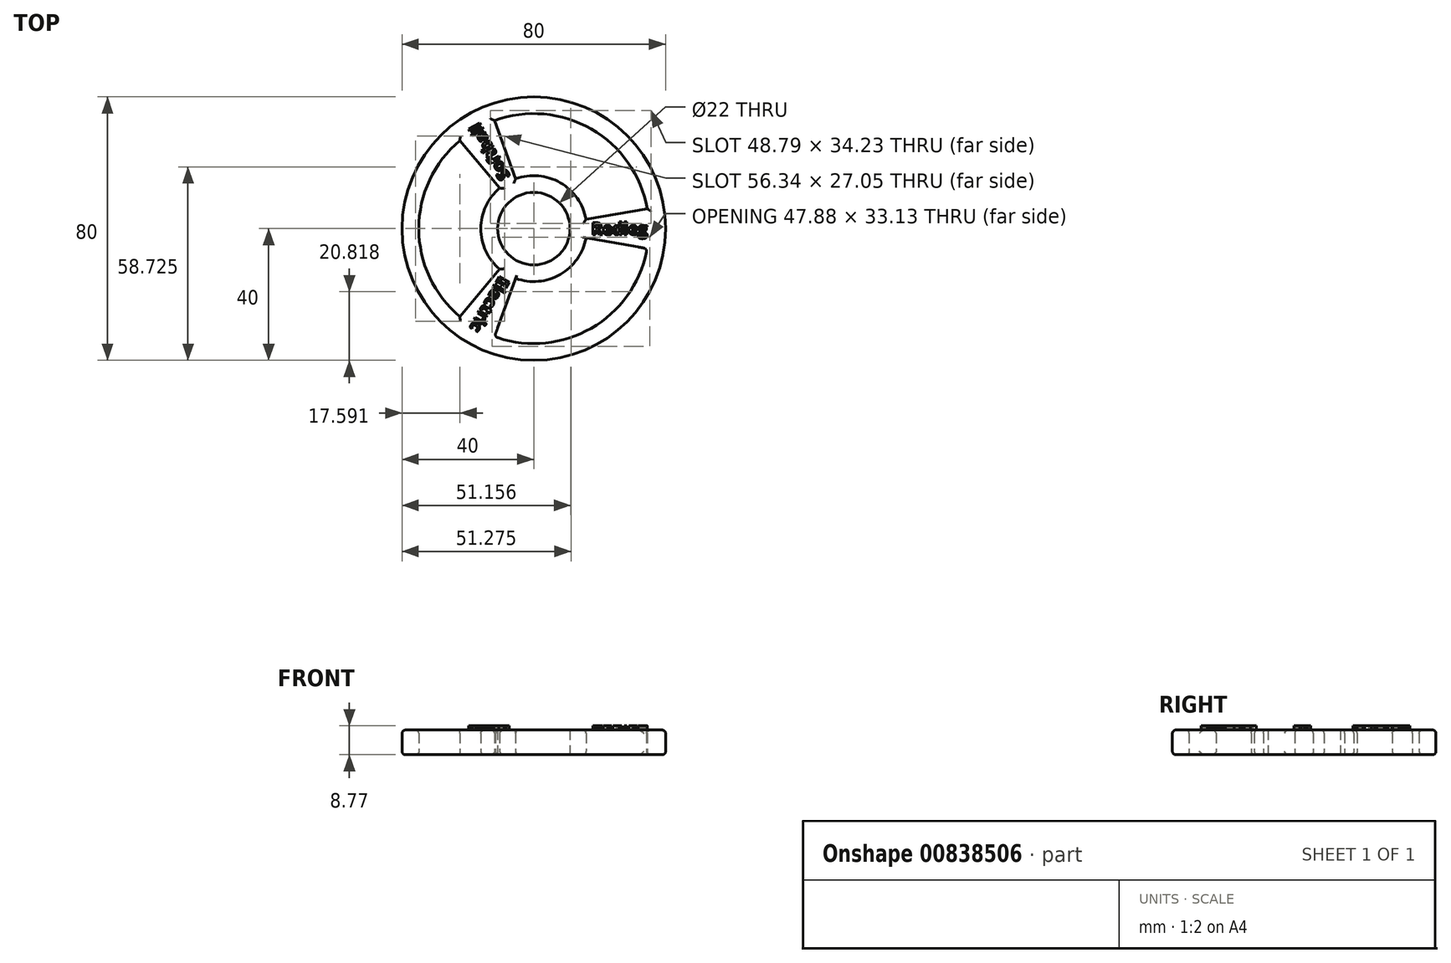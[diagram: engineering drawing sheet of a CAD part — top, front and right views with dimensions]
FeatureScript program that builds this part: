
annotation { "Feature Type Name" : "Feature", "Feature Type Description" : "" }
export const myFeature = defineFeature(function(context is Context, id is Id, definition is map)
    precondition{}
    {
        {
            var Q0;
            Q0=qCreatedBy(makeId("Top.planeOp"),FACE);
            var sketch = newSketch(context, id + "F0", { "sketchPlane" : qUnion([Q0])});
            skCircle(sketch, "E0", {"center": v(0, 0) * mm, "radius": 11 * mm});
            skCircle(sketch, "E1", {"center": v(0, 0) * mm, "radius": 16.08 * mm});
            skCircle(sketch, "E2", {"center": v(0, 0) * mm, "radius": 40 * mm});
            skCircle(sketch, "E3", {"center": v(0, 0) * mm, "radius": 34.92 * mm});
            skLineSegment(sketch, "E4", {"start": v(0, 0) * mm, "end": v(39.4, 6.95) * mm});
            skLineSegment(sketch, "E5.MirrorCS", {"start": v(0, 0) * mm, "end": v(39.4, -6.95) * mm});
            skLineSegment(sketch, "E6.1.0", {"start": v(0, 0) * mm, "end": v(-13.68, -37.59) * mm});
            skLineSegment(sketch, "E6.1.1", {"start": v(0, 0) * mm, "end": v(-25.71, -30.64) * mm});
            skLineSegment(sketch, "E6.2.0", {"start": v(0, 0) * mm, "end": v(-25.71, 30.64) * mm});
            skLineSegment(sketch, "E6.2.1", {"start": v(0, 0) * mm, "end": v(-13.68, 37.59) * mm});
            skLineSegment(sketch, "E6.anchor1", {"start": v(0, 0) * mm, "end": v(39.4, -6.95) * mm, "construction": true});
            skLineSegment(sketch, "E6.anchor2", {"start": v(0, 0) * mm, "end": v(-13.68, 37.59) * mm, "construction": true});
            skSolve(sketch);
        }
        {
            var Q0;
            {var subQ0=sQuery(id+"F0.wireOp",EDGE,"E6.2.0");var subQ1=sQuery(id+"F0.wireOp",EDGE,"E2");var subQ2=makeQuery(id+"F0.imprint","INTERSECT",VERTEX,{"derivedFrom":[subQ1,subQ0]});Q0=makeQuery(id+"F0.imprint","IMPRINT",FACE,{"disambiguationData":[TD([[makeQuery(id+"F0.imprint","IMPRINT",EDGE,{"disambiguationData":[TD([[subQ2,1.0]])],"derivedFrom":subQ1}),1.0]])]});}
            var Q1;
            {var subQ0=sQuery(id+"F0.wireOp",EDGE,"E6.1.1");var subQ1=sQuery(id+"F0.wireOp",EDGE,"E2");var subQ2=makeQuery(id+"F0.imprint","INTERSECT",VERTEX,{"derivedFrom":[subQ1,subQ0]});Q1=makeQuery(id+"F0.imprint","IMPRINT",FACE,{"disambiguationData":[TD([[makeQuery(id+"F0.imprint","IMPRINT",EDGE,{"disambiguationData":[TD([[subQ2,1.0]])],"derivedFrom":subQ1}),1.0]])]});}
            var Q2;
            {var subQ0=sQuery(id+"F0.wireOp",EDGE,"E4");var subQ1=sQuery(id+"F0.wireOp",EDGE,"E2");var subQ2=makeQuery(id+"F0.imprint","INTERSECT",VERTEX,{"derivedFrom":[subQ1,subQ0]});Q2=makeQuery(id+"F0.imprint","IMPRINT",FACE,{"disambiguationData":[TD([[makeQuery(id+"F0.imprint","IMPRINT",EDGE,{"disambiguationData":[TD([[subQ2,-1.0]])],"derivedFrom":subQ1}),1.0]])]});}
            var Q3;
            {var subQ0=sQuery(id+"F0.wireOp",EDGE,"E4");var subQ1=sQuery(id+"F0.wireOp",EDGE,"E2");var subQ2=makeQuery(id+"F0.imprint","INTERSECT",VERTEX,{"derivedFrom":[subQ1,subQ0]});Q3=makeQuery(id+"F0.imprint","IMPRINT",FACE,{"disambiguationData":[TD([[makeQuery(id+"F0.imprint","IMPRINT",EDGE,{"disambiguationData":[TD([[subQ2,1.0]])],"derivedFrom":subQ1}),1.0]])]});}
            var Q4;
            {var subQ0=sQuery(id+"F0.wireOp",EDGE,"E4");var subQ1=sQuery(id+"F0.wireOp",EDGE,"E1");var subQ2=makeQuery(id+"F0.imprint","INTERSECT",VERTEX,{"derivedFrom":[subQ1,subQ0]});Q4=makeQuery(id+"F0.imprint","IMPRINT",FACE,{"disambiguationData":[TD([[makeQuery(id+"F0.imprint","IMPRINT",EDGE,{"disambiguationData":[TD([[subQ2,1.0]])],"derivedFrom":subQ1}),-1.0]])]});}
            var Q5;
            {var subQ0=sQuery(id+"F0.wireOp",EDGE,"E4");var subQ1=sQuery(id+"F0.wireOp",EDGE,"E0");var subQ2=makeQuery(id+"F0.imprint","INTERSECT",VERTEX,{"derivedFrom":[subQ1,subQ0]});Q5=makeQuery(id+"F0.imprint","IMPRINT",FACE,{"disambiguationData":[TD([[makeQuery(id+"F0.imprint","IMPRINT",EDGE,{"disambiguationData":[TD([[subQ2,1.0]])],"derivedFrom":subQ1}),-1.0]])]});}
            var Q6;
            {var subQ0=sQuery(id+"F0.wireOp",EDGE,"E6.2.1");var subQ1=sQuery(id+"F0.wireOp",EDGE,"E0");var subQ2=makeQuery(id+"F0.imprint","INTERSECT",VERTEX,{"derivedFrom":[subQ1,subQ0]});Q6=makeQuery(id+"F0.imprint","IMPRINT",FACE,{"disambiguationData":[TD([[makeQuery(id+"F0.imprint","IMPRINT",EDGE,{"disambiguationData":[TD([[subQ2,1.0]])],"derivedFrom":subQ1}),-1.0]])]});}
            var Q7;
            {var subQ0=sQuery(id+"F0.wireOp",EDGE,"E6.2.1");var subQ1=sQuery(id+"F0.wireOp",EDGE,"E0");var subQ2=makeQuery(id+"F0.imprint","INTERSECT",VERTEX,{"derivedFrom":[subQ1,subQ0]});Q7=makeQuery(id+"F0.imprint","IMPRINT",FACE,{"disambiguationData":[TD([[makeQuery(id+"F0.imprint","IMPRINT",EDGE,{"disambiguationData":[TD([[subQ2,-1.0]])],"derivedFrom":subQ1}),-1.0]])]});}
            var Q8;
            {var subQ0=sQuery(id+"F0.wireOp",EDGE,"E6.2.1");var subQ1=sQuery(id+"F0.wireOp",EDGE,"E1");var subQ2=makeQuery(id+"F0.imprint","INTERSECT",VERTEX,{"derivedFrom":[subQ1,subQ0]});Q8=makeQuery(id+"F0.imprint","IMPRINT",FACE,{"disambiguationData":[TD([[makeQuery(id+"F0.imprint","IMPRINT",EDGE,{"disambiguationData":[TD([[subQ2,-1.0]])],"derivedFrom":subQ1}),-1.0]])]});}
            var Q9;
            {var subQ0=sQuery(id+"F0.wireOp",EDGE,"E6.2.0");var subQ1=sQuery(id+"F0.wireOp",EDGE,"E0");var subQ2=makeQuery(id+"F0.imprint","INTERSECT",VERTEX,{"derivedFrom":[subQ1,subQ0]});Q9=makeQuery(id+"F0.imprint","IMPRINT",FACE,{"disambiguationData":[TD([[makeQuery(id+"F0.imprint","IMPRINT",EDGE,{"disambiguationData":[TD([[subQ2,-1.0]])],"derivedFrom":subQ1}),-1.0]])]});}
            var Q10;
            {var subQ0=sQuery(id+"F0.wireOp",EDGE,"E6.1.1");var subQ1=sQuery(id+"F0.wireOp",EDGE,"E0");var subQ2=makeQuery(id+"F0.imprint","INTERSECT",VERTEX,{"derivedFrom":[subQ1,subQ0]});Q10=makeQuery(id+"F0.imprint","IMPRINT",FACE,{"disambiguationData":[TD([[makeQuery(id+"F0.imprint","IMPRINT",EDGE,{"disambiguationData":[TD([[subQ2,-1.0]])],"derivedFrom":subQ1}),-1.0]])]});}
            var Q11;
            {var subQ0=sQuery(id+"F0.wireOp",EDGE,"E6.1.0");var subQ1=sQuery(id+"F0.wireOp",EDGE,"E0");var subQ2=makeQuery(id+"F0.imprint","INTERSECT",VERTEX,{"derivedFrom":[subQ1,subQ0]});Q11=makeQuery(id+"F0.imprint","IMPRINT",FACE,{"disambiguationData":[TD([[makeQuery(id+"F0.imprint","IMPRINT",EDGE,{"disambiguationData":[TD([[subQ2,-1.0]])],"derivedFrom":subQ1}),-1.0]])]});}
            var Q12;
            {var subQ0=sQuery(id+"F0.wireOp",EDGE,"E6.1.1");var subQ1=sQuery(id+"F0.wireOp",EDGE,"E1");var subQ2=makeQuery(id+"F0.imprint","INTERSECT",VERTEX,{"derivedFrom":[subQ1,subQ0]});Q12=makeQuery(id+"F0.imprint","IMPRINT",FACE,{"disambiguationData":[TD([[makeQuery(id+"F0.imprint","IMPRINT",EDGE,{"disambiguationData":[TD([[subQ2,-1.0]])],"derivedFrom":subQ1}),-1.0]])]});}
            var Q13;
            {var subQ0=sQuery(id+"F0.wireOp",EDGE,"E6.1.0");var subQ1=sQuery(id+"F0.wireOp",EDGE,"E2");var subQ2=makeQuery(id+"F0.imprint","INTERSECT",VERTEX,{"derivedFrom":[subQ1,subQ0]});Q13=makeQuery(id+"F0.imprint","IMPRINT",FACE,{"disambiguationData":[TD([[makeQuery(id+"F0.imprint","IMPRINT",EDGE,{"disambiguationData":[TD([[subQ2,1.0]])],"derivedFrom":subQ1}),1.0]])]});}
            var Q14;
            {var subQ0=sQuery(id+"F0.wireOp",EDGE,"E5.MirrorCS");var subQ1=sQuery(id+"F0.wireOp",EDGE,"E2");var subQ2=makeQuery(id+"F0.imprint","INTERSECT",VERTEX,{"derivedFrom":[subQ1,subQ0]});Q14=makeQuery(id+"F0.imprint","IMPRINT",FACE,{"disambiguationData":[TD([[makeQuery(id+"F0.imprint","IMPRINT",EDGE,{"disambiguationData":[TD([[subQ2,1.0]])],"derivedFrom":subQ1}),1.0]])]});}
            extrude(context, id + "F1", {"entities" : qUnion([Q0, Q1, Q2, Q3, Q4, Q5, Q6, Q7, Q8, Q9, Q10, Q11, Q12, Q13, Q14]), "depth" : 7.5 * mm, "offsetDistance" : 25.4 * mm});
        }
        {
            var Q0;
            Q0=makeQuery(id+"F1.opExtrude","CAP_FACE",FACE,{"disambiguationData":[OSD([sQuery(id+"F0.wireOp",EDGE,"E0"),sQuery(id+"F0.wireOp",EDGE,"E1"),sQuery(id+"F0.wireOp",EDGE,"E2"),sQuery(id+"F0.wireOp",EDGE,"E3"),sQuery(id+"F0.wireOp",EDGE,"E4"),sQuery(id+"F0.wireOp",EDGE,"E5.MirrorCS"),sQuery(id+"F0.wireOp",EDGE,"E6.1.0"),sQuery(id+"F0.wireOp",EDGE,"E6.1.1"),sQuery(id+"F0.wireOp",EDGE,"E6.2.0"),sQuery(id+"F0.wireOp",EDGE,"E6.2.1")])],"isStart":false});
            var sketch = newSketch(context, id + "F2", { "sketchPlane" : qUnion([Q0])});
            skText(sketch, "E7", { "text": "Electric", "fontName": "OpenSans-Bold.ttf"});
            const initialGuessF2  = {"E7": [0.01744, -0.00186, 1, 0, 0.00362]};
            skSetInitialGuess(sketch, initialGuessF2);
            skSolve(sketch);
        }
        {
            var Q0;
            Q0 = qSketchRegion(id + "F2", true);
            extrude(context, id + "F3", {"entities" : qUnion([Q0]), "operationType" : NewBodyOperationType.ADD, "depth" : 1.27 * mm, "offsetDistance" : 25.4 * mm});
        }
        {
            var Q0;
            Q0=makeQuery(id+"F1.opExtrude","SWEPT_BODY",BODY,{"disambiguationData":[OSD([sQuery(id+"F0.wireOp",EDGE,"E0"),sQuery(id+"F0.wireOp",EDGE,"E1"),sQuery(id+"F0.wireOp",EDGE,"E2"),sQuery(id+"F0.wireOp",EDGE,"E3"),sQuery(id+"F0.wireOp",EDGE,"E4"),sQuery(id+"F0.wireOp",EDGE,"E5.MirrorCS"),sQuery(id+"F0.wireOp",EDGE,"E6.1.0"),sQuery(id+"F0.wireOp",EDGE,"E6.1.1"),sQuery(id+"F0.wireOp",EDGE,"E6.2.0"),sQuery(id+"F0.wireOp",EDGE,"E6.2.1")])]});
            var Q1;
            Q1=makeQuery(id+"F1.opExtrude","SWEPT_FACE",FACE,{"disambiguationData":[OSD([sQuery(id+"F0.wireOp",EDGE,"E2")])]});
            transform(context, id + "F4", {"entities" : qUnion([Q0]), "transformType" : TransformType.ROTATION, "transformAxis" : qUnion([Q1]), "angle" : 120 * degree, "oppositeDirection" : true, "makeCopy" : false});
        }
        {
            var Q0;
            Q0=makeQuery(id+"F2.imprint","IMPRINT",FACE,{"disambiguationData":[TD([[makeQuery(id+"F2.imprint","IMPRINT",EDGE,{"derivedFrom":sQuery(id+"F2.wireOp",EDGE,"E7.sketch_text.stroke-0")}),1.0]])]});
            var sketch = newSketch(context, id + "F5", { "sketchPlane" : qUnion([Q0])});
            skText(sketch, "E8", { "text": "Softball", "fontName": "OpenSans-Bold.ttf"});
            const initialGuessF5  = {"E8": [0.01741, -0.00178, 1, 0, 0.00357]};
            skSetInitialGuess(sketch, initialGuessF5);
            skSolve(sketch);
        }
        {
            var Q0;
            Q0 = qSketchRegion(id + "F5", true);
            extrude(context, id + "F6", {"entities" : qUnion([Q0]), "operationType" : NewBodyOperationType.ADD, "depth" : 1.27 * mm, "offsetDistance" : 25.4 * mm});
        }
        {
            var Q0;
            Q0=makeQuery(id+"F1.opExtrude","SWEPT_BODY",BODY,{"disambiguationData":[OSD([sQuery(id+"F0.wireOp",EDGE,"E0"),sQuery(id+"F0.wireOp",EDGE,"E1"),sQuery(id+"F0.wireOp",EDGE,"E2"),sQuery(id+"F0.wireOp",EDGE,"E3"),sQuery(id+"F0.wireOp",EDGE,"E4"),sQuery(id+"F0.wireOp",EDGE,"E5.MirrorCS"),sQuery(id+"F0.wireOp",EDGE,"E6.1.0"),sQuery(id+"F0.wireOp",EDGE,"E6.1.1"),sQuery(id+"F0.wireOp",EDGE,"E6.2.0"),sQuery(id+"F0.wireOp",EDGE,"E6.2.1")])]});
            var Q1;
            Q1=makeQuery(id+"F1.opExtrude","SWEPT_FACE",FACE,{"disambiguationData":[OSD([sQuery(id+"F0.wireOp",EDGE,"E2")])]});
            transform(context, id + "F7", {"entities" : qUnion([Q0]), "transformType" : TransformType.ROTATION, "transformAxis" : qUnion([Q1]), "angle" : 120 * degree, "oppositeDirection" : true, "makeCopy" : false});
        }
        {
            var Q0;
            Q0=makeQuery(id+"F2.imprint","IMPRINT",FACE,{"disambiguationData":[TD([[makeQuery(id+"F2.imprint","IMPRINT",EDGE,{"derivedFrom":sQuery(id+"F2.wireOp",EDGE,"E7.sketch_text.stroke-0")}),1.0]])]});
            var sketch = newSketch(context, id + "F8", { "sketchPlane" : qUnion([Q0])});
            skText(sketch, "E9", { "text": "Redleg", "fontName": "OpenSans-Bold.ttf"});
            const initialGuessF8  = {"E9": [0.01746, -0.00184, 1, 0, 0.00368]};
            skSetInitialGuess(sketch, initialGuessF8);
            skSolve(sketch);
        }
        {
            var Q0;
            Q0 = qSketchRegion(id + "F8", true);
            extrude(context, id + "F9", {"entities" : qUnion([Q0]), "operationType" : NewBodyOperationType.ADD, "depth" : 1.27 * mm, "offsetDistance" : 25.4 * mm});
        }
        {
            var Q0;
            {var subQ0=sQuery(id+"F0.wireOp",EDGE,"E3");Q0=makeQuery(id+"F1.opExtrude","CAP_EDGE",EDGE,{"disambiguationData":[OSD([subQ0]),TDD([makeQuery(id+"F0.imprint","IMPRINT",EDGE,{"disambiguationData":[TD([[makeQuery(id+"F0.imprint","INTERSECT",VERTEX,{"derivedFrom":[subQ0,sQuery(id+"F0.wireOp",EDGE,"E6.1.0")]}),-1.0]])],"derivedFrom":subQ0})])],"isStart":false});}
            var Q1;
            {var subQ0=sQuery(id+"F0.wireOp",EDGE,"E3");Q1=makeQuery(id+"F1.opExtrude","SWEPT_FACE",FACE,{"disambiguationData":[OSD([subQ0]),TDD([makeQuery(id+"F0.imprint","IMPRINT",EDGE,{"disambiguationData":[TD([[makeQuery(id+"F0.imprint","INTERSECT",VERTEX,{"derivedFrom":[subQ0,sQuery(id+"F0.wireOp",EDGE,"E6.2.1")]}),1.0]])],"derivedFrom":subQ0})])]});}
            var Q2;
            {var subQ0=sQuery(id+"F0.wireOp",EDGE,"E1");Q2=makeQuery(id+"F1.opExtrude","CAP_EDGE",EDGE,{"disambiguationData":[OSD([subQ0]),TDD([makeQuery(id+"F0.imprint","IMPRINT",EDGE,{"disambiguationData":[TD([[makeQuery(id+"F0.imprint","INTERSECT",VERTEX,{"derivedFrom":[subQ0,sQuery(id+"F0.wireOp",EDGE,"E6.2.0")]}),-1.0]])],"derivedFrom":subQ0})])],"isStart":false});}
            var Q3;
            {var subQ0=sQuery(id+"F0.wireOp",EDGE,"E1");Q3=makeQuery(id+"F1.opExtrude","CAP_EDGE",EDGE,{"disambiguationData":[OSD([subQ0]),TDD([makeQuery(id+"F0.imprint","IMPRINT",EDGE,{"disambiguationData":[TD([[makeQuery(id+"F0.imprint","INTERSECT",VERTEX,{"derivedFrom":[subQ0,sQuery(id+"F0.wireOp",EDGE,"E6.1.0")]}),-1.0]])],"derivedFrom":subQ0})])],"isStart":false});}
            var Q4;
            {var subQ0=sQuery(id+"F0.wireOp",EDGE,"E1");Q4=makeQuery(id+"F1.opExtrude","CAP_EDGE",EDGE,{"disambiguationData":[OSD([subQ0]),TDD([makeQuery(id+"F0.imprint","IMPRINT",EDGE,{"disambiguationData":[TD([[makeQuery(id+"F0.imprint","INTERSECT",VERTEX,{"derivedFrom":[subQ0,sQuery(id+"F0.wireOp",EDGE,"E6.2.1")]}),1.0]])],"derivedFrom":subQ0})])],"isStart":false});}
            var Q5;
            Q5=makeQuery(id+"F1.opExtrude","CAP_EDGE",EDGE,{"disambiguationData":[OSD([sQuery(id+"F0.wireOp",EDGE,"E6.1.1")])],"isStart":false});
            var Q6;
            Q6=makeQuery(id+"F1.opExtrude","CAP_EDGE",EDGE,{"disambiguationData":[OSD([sQuery(id+"F0.wireOp",EDGE,"E6.1.0")])],"isStart":false});
            var Q7;
            Q7=makeQuery(id+"F1.opExtrude","CAP_EDGE",EDGE,{"disambiguationData":[OSD([sQuery(id+"F0.wireOp",EDGE,"E6.2.0")])],"isStart":false});
            var Q8;
            {var subQ0=sQuery(id+"F0.wireOp",EDGE,"E3");Q8=makeQuery(id+"F1.opExtrude","CAP_EDGE",EDGE,{"disambiguationData":[OSD([subQ0]),TDD([makeQuery(id+"F0.imprint","IMPRINT",EDGE,{"disambiguationData":[TD([[makeQuery(id+"F0.imprint","INTERSECT",VERTEX,{"derivedFrom":[subQ0,sQuery(id+"F0.wireOp",EDGE,"E6.2.0")]}),-1.0]])],"derivedFrom":subQ0})])],"isStart":false});}
            var Q9;
            Q9=makeQuery(id+"F1.opExtrude","CAP_EDGE",EDGE,{"disambiguationData":[OSD([sQuery(id+"F0.wireOp",EDGE,"E2")])],"isStart":false});
            var Q10;
            Q10=makeQuery(id+"F1.opExtrude","CAP_EDGE",EDGE,{"disambiguationData":[OSD([sQuery(id+"F0.wireOp",EDGE,"E5.MirrorCS")])],"isStart":false});
            var Q11;
            {var subQ0=sQuery(id+"F0.wireOp",EDGE,"E3");Q11=makeQuery(id+"F1.opExtrude","CAP_EDGE",EDGE,{"disambiguationData":[OSD([subQ0]),TDD([makeQuery(id+"F0.imprint","IMPRINT",EDGE,{"disambiguationData":[TD([[makeQuery(id+"F0.imprint","INTERSECT",VERTEX,{"derivedFrom":[subQ0,sQuery(id+"F0.wireOp",EDGE,"E6.2.0")]}),-1.0]])],"derivedFrom":subQ0})])],"isStart":true});}
            var Q12;
            Q12=makeQuery(id+"F1.opExtrude","CAP_EDGE",EDGE,{"disambiguationData":[OSD([sQuery(id+"F0.wireOp",EDGE,"E2")])],"isStart":true});
            var Q13;
            Q13=makeQuery(id+"F1.opExtrude","CAP_EDGE",EDGE,{"disambiguationData":[OSD([sQuery(id+"F0.wireOp",EDGE,"E6.2.0")])],"isStart":true});
            var Q14;
            {var subQ0=sQuery(id+"F0.wireOp",EDGE,"E1");Q14=makeQuery(id+"F1.opExtrude","CAP_EDGE",EDGE,{"disambiguationData":[OSD([subQ0]),TDD([makeQuery(id+"F0.imprint","IMPRINT",EDGE,{"disambiguationData":[TD([[makeQuery(id+"F0.imprint","INTERSECT",VERTEX,{"derivedFrom":[subQ0,sQuery(id+"F0.wireOp",EDGE,"E6.1.0")]}),-1.0]])],"derivedFrom":subQ0})])],"isStart":true});}
            var Q15;
            Q15=makeQuery(id+"F1.opExtrude","CAP_EDGE",EDGE,{"disambiguationData":[OSD([sQuery(id+"F0.wireOp",EDGE,"E5.MirrorCS")])],"isStart":true});
            var Q16;
            {var subQ0=sQuery(id+"F0.wireOp",EDGE,"E3");Q16=makeQuery(id+"F1.opExtrude","CAP_EDGE",EDGE,{"disambiguationData":[OSD([subQ0]),TDD([makeQuery(id+"F0.imprint","IMPRINT",EDGE,{"disambiguationData":[TD([[makeQuery(id+"F0.imprint","INTERSECT",VERTEX,{"derivedFrom":[subQ0,sQuery(id+"F0.wireOp",EDGE,"E6.1.0")]}),-1.0]])],"derivedFrom":subQ0})])],"isStart":true});}
            var Q17;
            Q17=makeQuery(id+"F1.opExtrude","CAP_EDGE",EDGE,{"disambiguationData":[OSD([sQuery(id+"F0.wireOp",EDGE,"E6.1.0")])],"isStart":true});
            var Q18;
            Q18=makeQuery(id+"F1.opExtrude","CAP_EDGE",EDGE,{"disambiguationData":[OSD([sQuery(id+"F0.wireOp",EDGE,"E6.1.1")])],"isStart":true});
            var Q19;
            {var subQ0=sQuery(id+"F0.wireOp",EDGE,"E1");Q19=makeQuery(id+"F1.opExtrude","CAP_EDGE",EDGE,{"disambiguationData":[OSD([subQ0]),TDD([makeQuery(id+"F0.imprint","IMPRINT",EDGE,{"disambiguationData":[TD([[makeQuery(id+"F0.imprint","INTERSECT",VERTEX,{"derivedFrom":[subQ0,sQuery(id+"F0.wireOp",EDGE,"E6.2.0")]}),-1.0]])],"derivedFrom":subQ0})])],"isStart":true});}
            var Q20;
            {var subQ0=sQuery(id+"F0.wireOp",EDGE,"E1");Q20=makeQuery(id+"F1.opExtrude","CAP_EDGE",EDGE,{"disambiguationData":[OSD([subQ0]),TDD([makeQuery(id+"F0.imprint","IMPRINT",EDGE,{"disambiguationData":[TD([[makeQuery(id+"F0.imprint","INTERSECT",VERTEX,{"derivedFrom":[subQ0,sQuery(id+"F0.wireOp",EDGE,"E6.2.1")]}),1.0]])],"derivedFrom":subQ0})])],"isStart":true});}
            fillet(context, id + "F10", {"entities" : qUnion([Q0, Q1, Q2, Q3, Q4, Q5, Q6, Q7, Q8, Q9, Q10, Q11, Q12, Q13, Q14, Q15, Q16, Q17, Q18, Q19, Q20]), "radius" : 1.02 * mm, "tangentPropagation" : true, "allowEdgeOverflow" : false});
        }
    });
